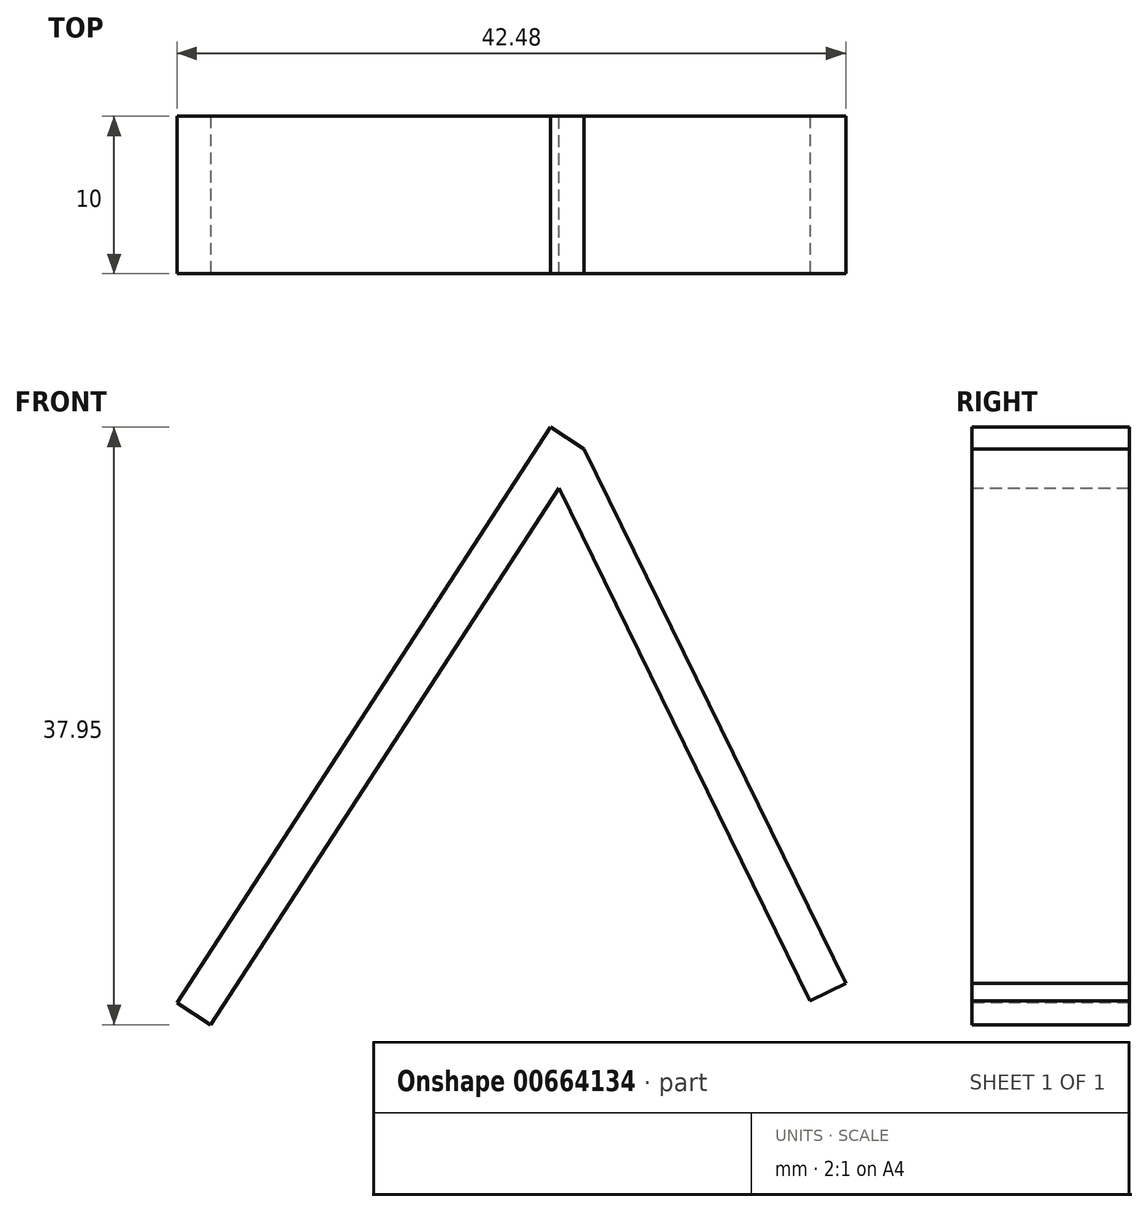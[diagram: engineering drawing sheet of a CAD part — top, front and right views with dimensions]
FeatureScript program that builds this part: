
annotation { "Feature Type Name" : "Feature", "Feature Type Description" : "" }
export const myFeature = defineFeature(function(context is Context, id is Id, definition is map)
    precondition{}
    {
        {
            var Q0;
            Q0=qCreatedBy(makeId("Front.planeOp"),FACE);
            var sketch = newSketch(context, id + "F0", { "sketchPlane" : qUnion([Q0])});
            skLineSegment(sketch, "E0", {"start": v(-52.69, -36.57) * mm, "end": v(-28.95, 0) * mm});
            skLineSegment(sketch, "E1", {"start": v(-28.95, 0) * mm, "end": v(-12.34, -33.94) * mm});
            skSolve(sketch);
        }
        {
            var Q0;
            Q0=sQuery(id+"F0.wireOp",EDGE,"E1");
            var Q1;
            Q1=sQuery(id+"F0.wireOp",EDGE,"E0");
            extrude(context, id + "F1", {"bodyType" : ToolBodyType.SURFACE, "surfaceEntities" : qUnion([Q0, Q1]), "depth" : 10 * mm, "offsetDistance" : 25.4 * mm});
        }
        {
            var Q0;
            Q0=makeQuery(id+"F1.opExtrude","SWEPT_FACE",FACE,{"disambiguationData":[OSD([sQuery(id+"F0.wireOp",EDGE,"E0")])]});
            extrude(context, id + "F2", {"entities" : qUnion([Q0]), "oppositeDirection" : true, "depth" : 2.54 * mm, "offsetDistance" : 25.4 * mm});
        }
        {
            var Q0;
            Q0=makeQuery(id+"F1.opExtrude","SWEPT_FACE",FACE,{"disambiguationData":[OSD([sQuery(id+"F0.wireOp",EDGE,"E1")])]});
            extrude(context, id + "F3", {"entities" : qUnion([Q0]), "operationType" : NewBodyOperationType.ADD, "depth" : 2.54 * mm, "offsetDistance" : 25.4 * mm});
        }
    });
